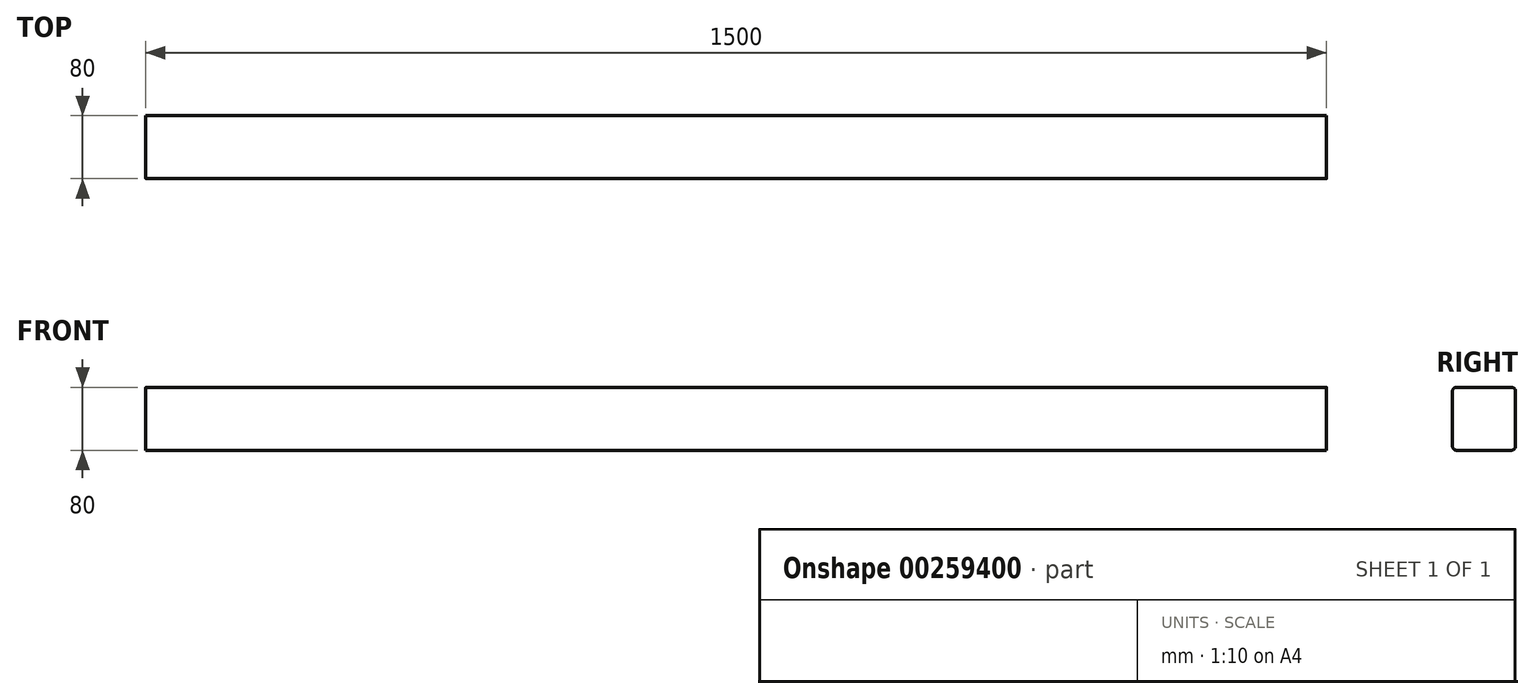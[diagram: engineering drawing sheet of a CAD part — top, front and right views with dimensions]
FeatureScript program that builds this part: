
annotation { "Feature Type Name" : "Feature", "Feature Type Description" : "" }
export const myFeature = defineFeature(function(context is Context, id is Id, definition is map)
    precondition{}
    {
        {
            var Q0;
            Q0=qCreatedBy(makeId("Right.planeOp"),FACE);
            var sketch = newSketch(context, id + "F0", { "sketchPlane" : qUnion([Q0])});
            skLineSegment(sketch, "E0.bottom", {"start": v(35, 40) * mm, "end": v(-35, 40) * mm});
            skLineSegment(sketch, "E0.top", {"start": v(35, -40) * mm, "end": v(-35, -40) * mm});
            skLineSegment(sketch, "E0.left", {"start": v(40, 35) * mm, "end": v(40, -35) * mm});
            skLineSegment(sketch, "E0.right", {"start": v(-40, 35) * mm, "end": v(-40, -35) * mm});
            skPoint(sketch, "E0.middle", {"position": v(0, 0) * mm});
            skPoint(sketch, "E1.visualSharp", {"position": v(-40, 40) * mm});
            skArc(sketch, "E1.filletArc", {"start": v(-35, 40) * mm, "mid": v(-38.54, 38.54) * mm, "end": v(-40, 35) * mm});
            skPoint(sketch, "E2.visualSharp", {"position": v(40, 40) * mm});
            skArc(sketch, "E2.filletArc", {"start": v(40, 35) * mm, "mid": v(38.54, 38.54) * mm, "end": v(35, 40) * mm});
            skPoint(sketch, "E3.visualSharp", {"position": v(40, -40) * mm});
            skArc(sketch, "E3.filletArc", {"start": v(35, -40) * mm, "mid": v(38.54, -38.54) * mm, "end": v(40, -35) * mm});
            skPoint(sketch, "E4.visualSharp", {"position": v(-40, -40) * mm});
            skArc(sketch, "E4.filletArc", {"start": v(-40, -35) * mm, "mid": v(-38.54, -38.54) * mm, "end": v(-35, -40) * mm});
            skSolve(sketch);
        }
        {
            var Q0;
            Q0=makeQuery(id+"F0.imprint","IMPRINT",FACE,{"disambiguationData":[TD([[makeQuery(id+"F0.imprint","IMPRINT",EDGE,{"derivedFrom":sQuery(id+"F0.wireOp",EDGE,"E0.bottom")}),1.0]])]});
            extrude(context, id + "F1", {"entities" : qUnion([Q0]), "depth" : 1500 * mm});
        }
    });
